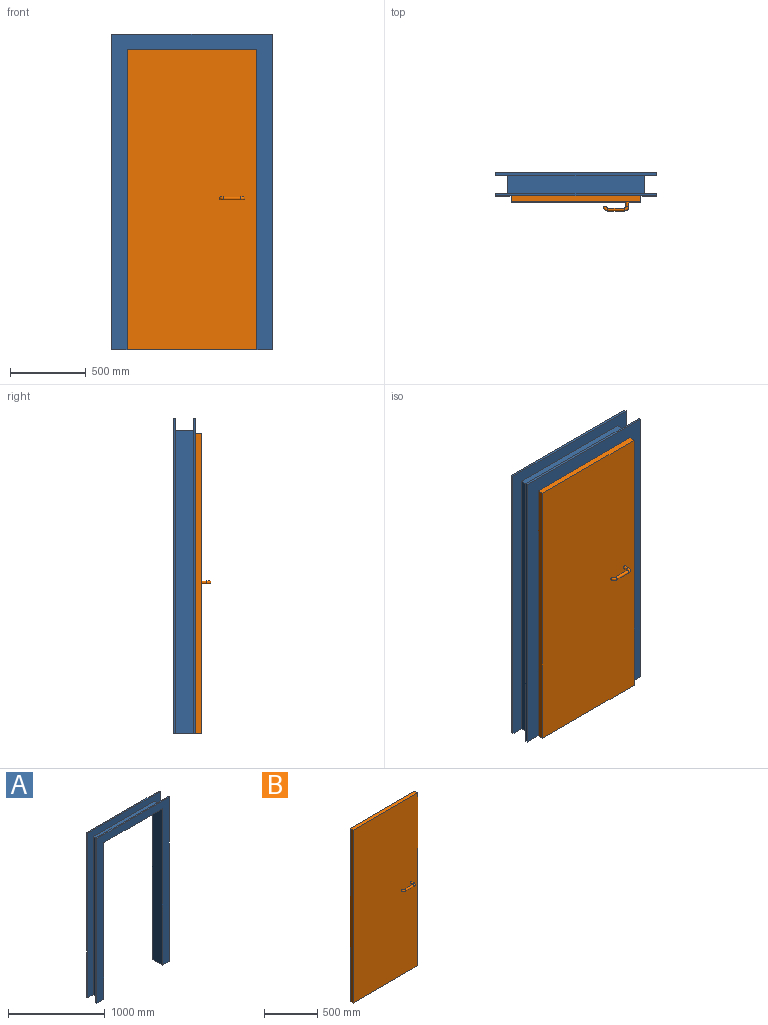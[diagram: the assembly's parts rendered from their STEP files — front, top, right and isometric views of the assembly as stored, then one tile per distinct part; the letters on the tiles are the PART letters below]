
ASSEMBLY  parts=2 mates=1
PART A: 18 faces, bbox 1060x150x2085 mm
  f0: plane 2085x15mm, normal (-1,0,0), area 31275mm2, adj f3,f5,f8,f15
  f1: plane 2085x15mm, normal (1,0,0), area 31275mm2, adj f3,f7,f8,f15
  f2: plane 900x120mm, normal (0,0,1), area 108000mm2, adj f14,f15,f16,f17
  f3: plane 1060x15mm, normal (0,0,1), area 15900mm2, adj f0,f1,f8,f15
  f4: plane 2085x15mm, normal (-1,0,0), area 31275mm2, adj f5,f6,f9,f14
  f5: plane 150x100mm, normal (0,0,-1), area 5400mm2, adj f0,f4,f6,f8,f11,f14,f15,f17
  f6: plane 2085x1060mm, normal (0,1,0), area 503000mm2, adj f4,f5,f7,f9,f10,f11,f12,f13
  f7: plane 150x100mm, normal (0,0,-1), area 5400mm2, adj f1,f6,f8,f10,f12,f14,f15,f16
  f8: plane 2085x1060mm, normal (0,-1,0), area 503000mm2, adj f0,f1,f3,f5,f7,f11,f12,f13
  f9: plane 1060x15mm, normal (0,0,1), area 15900mm2, adj f4,f6,f10,f14
  f10: plane 2085x15mm, normal (1,0,0), area 31275mm2, adj f6,f7,f9,f14
  f11: plane 1985x150mm, normal (1,0,0), area 297750mm2, adj f5,f6,f8,f13
  f12: plane 1985x150mm, normal (-1,0,0), area 297750mm2, adj f6,f7,f8,f13
  f13: plane 860x150mm, normal (0,0,-1), area 129000mm2, adj f6,f8,f11,f12
  f14: plane 2085x1060mm, normal (0,-1,0), area 405600mm2, adj f2,f4,f5,f7,f9,f10,f16,f17
  f15: plane 2085x1060mm, normal (0,1,0), area 405600mm2, adj f0,f1,f2,f3,f5,f7,f16,f17
  f16: plane 2005x120mm, normal (1,0,0), area 240600mm2, adj f2,f7,f14,f15
  f17: plane 2005x120mm, normal (-1,0,0), area 240600mm2, adj f2,f5,f14,f15
PART B: 11 faces, bbox 860x102.5x1985 mm
  f0: plane 1985x40mm, normal (-1,0,0), area 79400mm2, adj f1,f3,f4,f5
  f1: plane 860x40mm, normal (0,0,-1), area 34400mm2, adj f0,f2,f4,f5
  f2: plane 1985x40mm, normal (1,0,0), area 79400mm2, adj f1,f3,f4,f5
  f3: plane 860x40mm, normal (0,0,1), area 34400mm2, adj f0,f2,f4,f5
  f4: plane 1985x860mm, normal (0,-1,0), area 1706785.8mm2, adj f0,f1,f2,f3,f7
  f5: plane 1985x860mm, normal (0,1,0), area 1707100mm2, adj f0,f1,f2,f3
  f6: plane 20x20mm, normal (0,1,0), area 314.2mm2, adj f10
  f7: cylinder r=10mm len=30mm, axis (0,-1,0), area 1885mm2, adj f4,f8
  f8: torus R=20mm, axis (0,0,-1), area 1973.9mm2, adj f7,f9
  f9: cylinder r=10mm len=110mm, axis (-1,0,0), area 6911.5mm2, adj f8,f10
  f10: torus R=20mm, axis (0,0,-1), area 1973.9mm2, adj f6,f9
PLACE A t=(20,75,0)mm
PLACE B t=(20,-75,0)mm
MATE revolute B.f1 <-> A.f5  axis (0,0,-1) through (20,-75,0)mm
